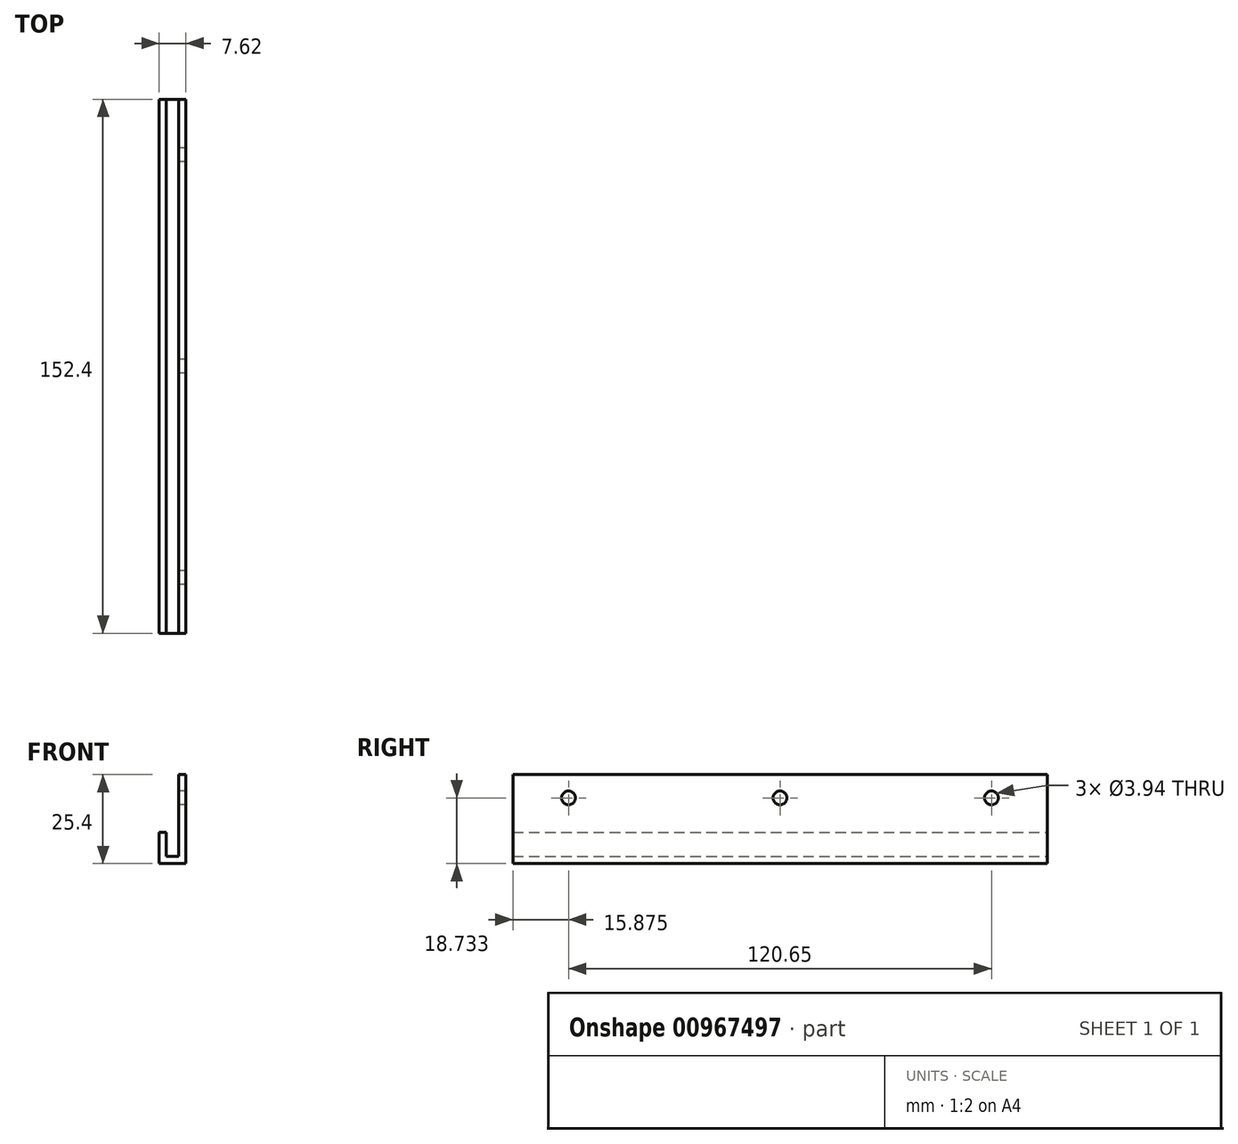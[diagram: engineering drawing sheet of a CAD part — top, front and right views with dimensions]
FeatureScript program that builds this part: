
annotation { "Feature Type Name" : "Feature", "Feature Type Description" : "" }
export const myFeature = defineFeature(function(context is Context, id is Id, definition is map)
    precondition{}
    {
        {
            var Q0;
            Q0=qCreatedBy(makeId("Front.planeOp"),FACE);
            var sketch = newSketch(context, id + "F0", { "sketchPlane" : qUnion([Q0])});
            skLineSegment(sketch, "E0", {"start": v(0, 25.4) * mm, "end": v(0, 0) * mm});
            skLineSegment(sketch, "E1", {"start": v(-7.62, 0) * mm, "end": v(-7.62, 8.9) * mm});
            skLineSegment(sketch, "E2", {"start": v(-7.62, 8.9) * mm, "end": v(-5.59, 8.9) * mm});
            skLineSegment(sketch, "E3", {"start": v(-5.59, 8.9) * mm, "end": v(-5.59, 2.03) * mm});
            skLineSegment(sketch, "E4", {"start": v(-5.59, 2.03) * mm, "end": v(-2.03, 2.03) * mm});
            skLineSegment(sketch, "E5", {"start": v(-2.03, 2.03) * mm, "end": v(-2.03, 25.4) * mm});
            skLineSegment(sketch, "E6", {"start": v(-2.03, 25.4) * mm, "end": v(0, 25.4) * mm});
            skLineSegment(sketch, "E7", {"start": v(0, 0) * mm, "end": v(-7.62, 0) * mm});
            skSolve(sketch);
        }
        {
            var Q0;
            Q0=makeQuery(id+"F0.imprint","IMPRINT",FACE,{"disambiguationData":[TD([[makeQuery(id+"F0.imprint","IMPRINT",EDGE,{"derivedFrom":sQuery(id+"F0.wireOp",EDGE,"E0")}),-1.0]])]});
            extrude(context, id + "F1", {"entities" : qUnion([Q0]), "endBound" : BoundingType.SYMMETRIC, "depth" : 152.4 * mm, "offsetDistance" : 25.4 * mm});
        }
        {
            var Q0;
            Q0=makeQuery(id+"F1.opExtrude","SWEPT_FACE",FACE,{"disambiguationData":[OSD([sQuery(id+"F0.wireOp",EDGE,"E5")])]});
            var sketch = newSketch(context, id + "F2", { "sketchPlane" : qUnion([Q0])});
            skCircle(sketch, "E8", {"center": v(0, 18.73) * mm, "radius": 1.97 * mm});
            skCircle(sketch, "E9", {"center": v(-60.33, 18.73) * mm, "radius": 1.97 * mm});
            skCircle(sketch, "E10", {"center": v(60.33, 18.73) * mm, "radius": 1.97 * mm});
            skSolve(sketch);
        }
        {
            var Q0;
            Q0=makeQuery(id+"F2.imprint","IMPRINT",FACE,{"disambiguationData":[TD([[makeQuery(id+"F2.imprint","IMPRINT",EDGE,{"derivedFrom":sQuery(id+"F2.wireOp",EDGE,"E9")}),1.0]])]});
            var Q1;
            Q1=makeQuery(id+"F2.imprint","IMPRINT",FACE,{"disambiguationData":[TD([[makeQuery(id+"F2.imprint","IMPRINT",EDGE,{"derivedFrom":sQuery(id+"F2.wireOp",EDGE,"E8")}),1.0]])]});
            var Q2;
            Q2=makeQuery(id+"F2.imprint","IMPRINT",FACE,{"disambiguationData":[TD([[makeQuery(id+"F2.imprint","IMPRINT",EDGE,{"derivedFrom":sQuery(id+"F2.wireOp",EDGE,"E10")}),1.0]])]});
            extrude(context, id + "F3", {"entities" : qUnion([Q0, Q1, Q2]), "operationType" : NewBodyOperationType.REMOVE, "endBound" : BoundingType.THROUGH_ALL, "oppositeDirection" : true, "depth" : 25.4 * mm, "offsetDistance" : 25.4 * mm});
        }
    });
